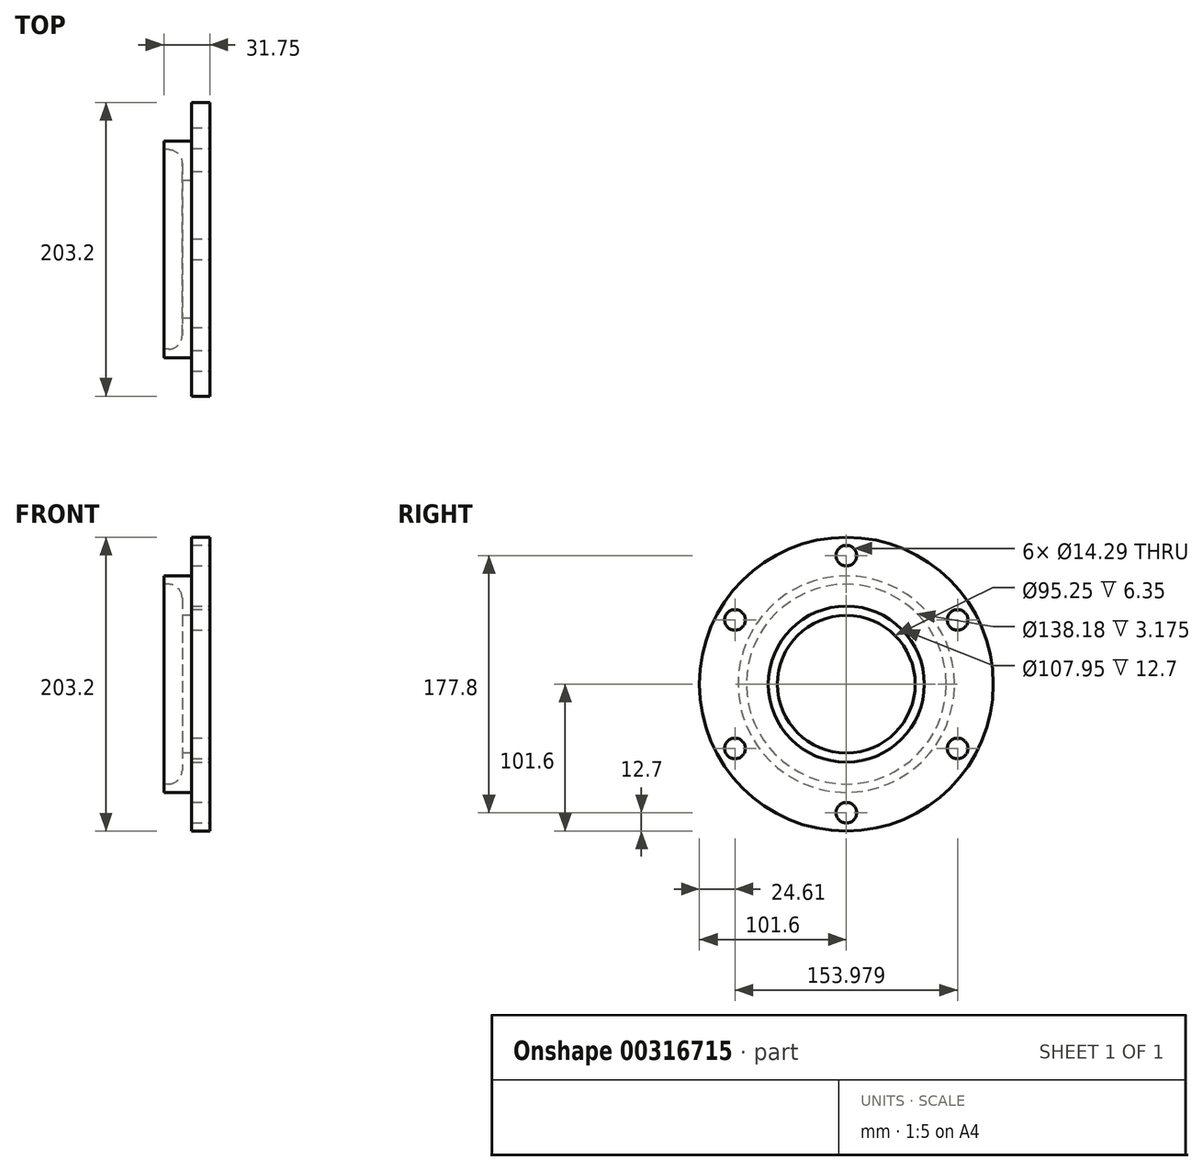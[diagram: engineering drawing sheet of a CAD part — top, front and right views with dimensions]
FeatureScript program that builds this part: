
annotation { "Feature Type Name" : "Feature", "Feature Type Description" : "" }
export const myFeature = defineFeature(function(context is Context, id is Id, definition is map)
    precondition{}
    {
        {
            var Q0;
            Q0=qCreatedBy(makeId("Right.planeOp"),FACE);
            var sketch = newSketch(context, id + "F0", { "sketchPlane" : qUnion([Q0])});
            skCircle(sketch, "E0", {"center": v(0, 0) * mm, "radius": 101.6 * mm});
            skSolve(sketch);
        }
        {
            var Q0;
            Q0 = qSketchRegion(id + "F0", true);
            extrude(context, id + "F1", {"entities" : qUnion([Q0]), "depth" : 12.7 * mm});
        }
        {
            var Q0;
            Q0=makeQuery(id+"F1.opExtrude","CAP_FACE",FACE,{"disambiguationData":[OSD([sQuery(id+"F0.wireOp",EDGE,"E0")])],"isStart":true});
            var sketch = newSketch(context, id + "F2", { "sketchPlane" : qUnion([Q0])});
            skCircle(sketch, "E1", {"center": v(0, 0) * mm, "radius": 74.87 * mm});
            skSolve(sketch);
        }
        {
            var Q0;
            Q0 = qSketchRegion(id + "F2", true);
            extrude(context, id + "F3", {"entities" : qUnion([Q0]), "operationType" : NewBodyOperationType.ADD, "depth" : 19.05 * mm});
        }
        {
            var Q0;
            Q0=makeQuery(id+"F3.opExtrude","CAP_FACE",FACE,{"disambiguationData":[OSD([sQuery(id+"F2.wireOp",EDGE,"E1")])],"isStart":false});
            var sketch = newSketch(context, id + "F4", { "sketchPlane" : qUnion([Q0])});
            skCircle(sketch, "E2", {"center": v(0, 0) * mm, "radius": 69.09 * mm});
            skSolve(sketch);
        }
        {
            var Q0;
            Q0 = qSketchRegion(id + "F4", true);
            extrude(context, id + "F5", {"entities" : qUnion([Q0]), "operationType" : NewBodyOperationType.REMOVE, "oppositeDirection" : true, "depth" : 12.7 * mm});
        }
        {
            var Q0;
            Q0=makeQuery(id+"F5.boolean.opBoolean","COPY",EDGE,{"derivedFrom":makeQuery(id+"F5.opExtrude","CAP_EDGE",EDGE,{"disambiguationData":[OSD([sQuery(id+"F4.wireOp",EDGE,"E2")])],"isStart":false})});
            fillet(context, id + "F6", {"entities" : qUnion([Q0]), "radius" : 9.52 * mm, "tangentPropagation" : true, "allowEdgeOverflow" : false});
        }
        {
            var Q0;
            Q0=makeQuery(id+"F5.boolean.opBoolean","COPY",FACE,{"derivedFrom":makeQuery(id+"F5.opExtrude","CAP_FACE",FACE,{"disambiguationData":[OSD([sQuery(id+"F4.wireOp",EDGE,"E2")])],"isStart":false})});
            var sketch = newSketch(context, id + "F7", { "sketchPlane" : qUnion([Q0])});
            skCircle(sketch, "E3", {"center": v(0, 0) * mm, "radius": 47.63 * mm});
            skSolve(sketch);
        }
        {
            var Q0;
            Q0 = qSketchRegion(id + "F7", true);
            extrude(context, id + "F8", {"entities" : qUnion([Q0]), "operationType" : NewBodyOperationType.REMOVE, "endBound" : BoundingType.THROUGH_ALL, "oppositeDirection" : true, "depth" : 25.4 * mm});
        }
        {
            var Q0;
            Q0=makeQuery(id+"F1.opExtrude","CAP_FACE",FACE,{"disambiguationData":[OSD([sQuery(id+"F0.wireOp",EDGE,"E0")])],"isStart":false});
            var sketch = newSketch(context, id + "F9", { "sketchPlane" : qUnion([Q0])});
            skCircle(sketch, "E4", {"center": v(0, 0) * mm, "radius": 53.98 * mm});
            skSolve(sketch);
        }
        {
            var Q0;
            Q0 = qSketchRegion(id + "F9", true);
            extrude(context, id + "F10", {"entities" : qUnion([Q0]), "operationType" : NewBodyOperationType.REMOVE, "oppositeDirection" : true, "depth" : 12.7 * mm});
        }
        {
            var Q0;
            Q0=makeQuery(id+"F1.opExtrude","CAP_FACE",FACE,{"disambiguationData":[OSD([sQuery(id+"F0.wireOp",EDGE,"E0")])],"isStart":false});
            var sketch = newSketch(context, id + "F11", { "sketchPlane" : qUnion([Q0])});
            skCircle(sketch, "E5", {"center": v(0, 0) * mm, "radius": 88.9 * mm, "construction": true});
            skLineSegment(sketch, "E6", {"start": v(0, 0) * mm, "end": v(0, -120.17) * mm, "construction": true});
            skPoint(sketch, "E7", {"position": v(0, -88.9) * mm});
            skPoint(sketch, "E8.1.0", {"position": v(76.99, -44.45) * mm});
            skPoint(sketch, "E8.2.0", {"position": v(76.99, 44.45) * mm});
            skPoint(sketch, "E8.3.0", {"position": v(0, 88.9) * mm});
            skPoint(sketch, "E8.4.0", {"position": v(-76.99, 44.45) * mm});
            skPoint(sketch, "E8.5.0", {"position": v(-76.99, -44.45) * mm});
            skSolve(sketch);
        }
        {
            var Q0;
            Q0=sQuery(id+"F11.wireOp",VERTEX,"E7");
            var Q1;
            Q1=sQuery(id+"F11.wireOp",VERTEX,"E8.1.0");
            var Q2;
            Q2=sQuery(id+"F11.wireOp",VERTEX,"E8.2.0");
            var Q3;
            Q3=sQuery(id+"F11.wireOp",VERTEX,"E8.3.0");
            var Q4;
            Q4=sQuery(id+"F11.wireOp",VERTEX,"E8.4.0");
            var Q5;
            Q5=sQuery(id+"F11.wireOp",VERTEX,"E8.5.0");
            var Q6;
            Q6=makeQuery(id+"F1.opExtrude","SWEPT_BODY",BODY,{"disambiguationData":[OSD([sQuery(id+"F0.wireOp",EDGE,"E0")])]});
            hole(context, id + "F12", {"style" : HoleStyle.SIMPLE, "endStyle" : HoleEndStyle.THROUGH, "holeDiameter" : 14.29 * mm, "tappedDepth" : 21.59 * mm, "tapClearance" : 3, "locations" : qUnion([Q0, Q1, Q2, Q3, Q4, Q5]), "scope" : qUnion([Q6])});
        }
    });
